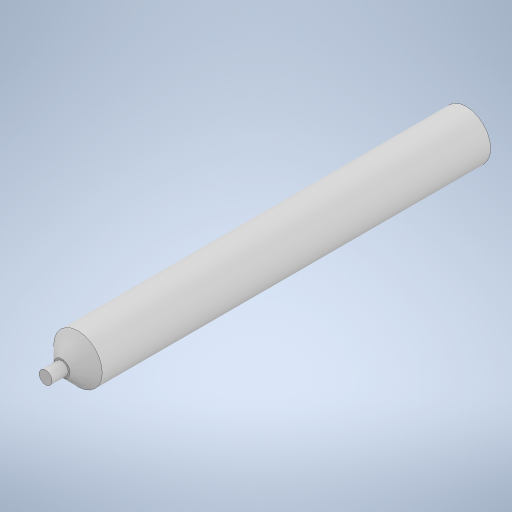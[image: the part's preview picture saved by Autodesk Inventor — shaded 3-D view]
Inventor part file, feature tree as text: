
AUTODESK INVENTOR PART (.ipt)
format: ipt  version: 2023 (Build 270158000, 158)  size: 235,008 bytes
history: native  units: in
note: dims shown in document units (in); Inventor stores cm internally (conversion verified against a paired STEP export)
features: extrude x2, sketch x2, chamfer x1
ambient origin geometry x8: Origin, YZ Plane, XZ Plane, XY Plane, X Axis, Y Axis, Z Axis, Center Point
bodies: Solid1 (feature_tree)
feature tree (5):
  extrude  "Extrusion1"  Depth=4.9213in TaperAngle=0.0deg
  extrude  "Extrusion2"  Depth=0.1969in TaperAngle=0.0deg
  chamfer  "Chamfer1"  Distance=0.1969in Angle=45.0deg
  sketch  "Sketch2"  dims[d0=0.5906in d1=4.9213in d2=0.0in]
  sketch  "Sketch3"  dims[d3=0.1575in d4=0.1969in d5=0.0in d6=0.1969in d7=0.0787in d8=45.0deg]
